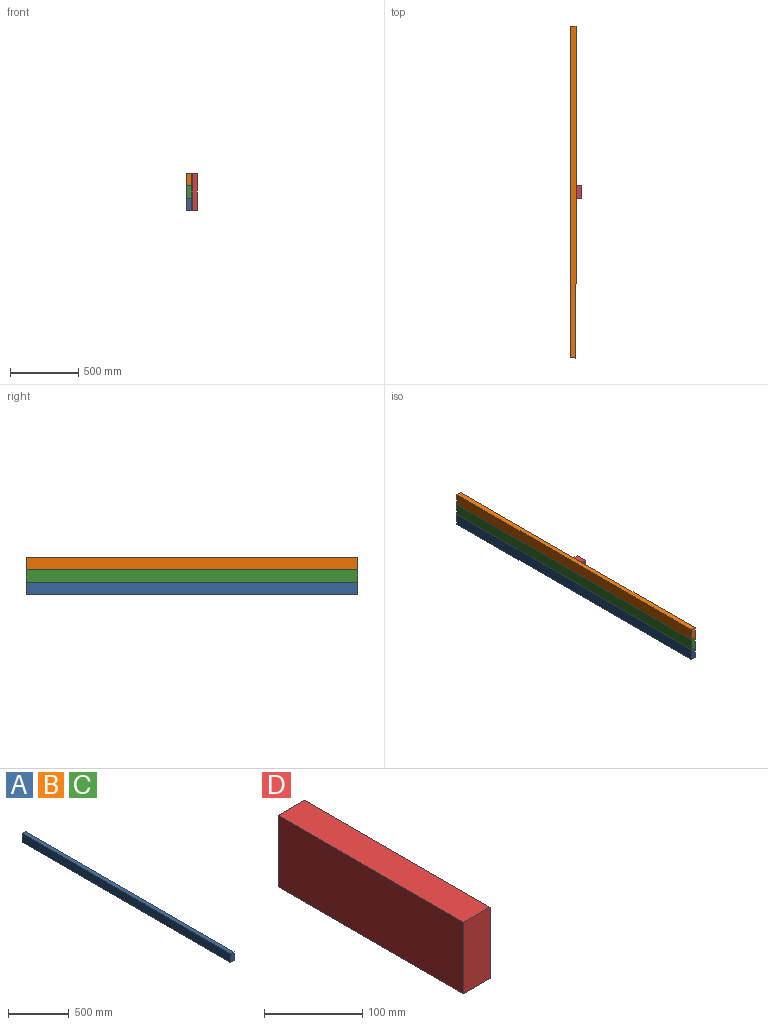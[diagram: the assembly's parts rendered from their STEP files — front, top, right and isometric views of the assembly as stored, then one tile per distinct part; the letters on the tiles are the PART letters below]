
ASSEMBLY  parts=4 mates=3
PART A: 6 faces, bbox 38.1x2438.4x88.9 mm
  f0: plane 2438.4x38.1mm, normal (0,0,1), area 92903mm2, adj f1,f3,f4,f5
  f1: plane 2438.4x88.9mm, normal (-1,0,0), area 216773.8mm2, adj f0,f2,f4,f5
  f2: plane 2438.4x38.1mm, normal (0,0,-1), area 92903mm2, adj f1,f3,f4,f5
  f3: plane 2438.4x88.9mm, normal (1,0,0), area 216773.8mm2, adj f0,f2,f4,f5
  f4: plane 88.9x38.1mm, normal (0,-1,0), area 3387.1mm2, adj f0,f1,f2,f3
  f5: plane 88.9x38.1mm, normal (0,1,0), area 3387.1mm2, adj f0,f1,f2,f3
PART B: same geometry as A
PART C: same geometry as A
PART D: 6 faces, bbox 38.1x266.7x88.9 mm
  f0: plane 266.7x38.1mm, normal (0,0,1), area 10161.3mm2, adj f1,f3,f4,f5
  f1: plane 266.7x88.9mm, normal (-1,0,0), area 23709.6mm2, adj f0,f2,f4,f5
  f2: plane 266.7x38.1mm, normal (0,0,-1), area 10161.3mm2, adj f1,f3,f4,f5
  f3: plane 266.7x88.9mm, normal (1,0,0), area 23709.6mm2, adj f0,f2,f4,f5
  f4: plane 88.9x38.1mm, normal (0,-1,0), area 3387.1mm2, adj f0,f1,f2,f3
  f5: plane 88.9x38.1mm, normal (0,1,0), area 3387.1mm2, adj f0,f1,f2,f3
PLACE A t=(-434.98,191.68,-159.44)mm
PLACE B rot(axis=(-1,0,0),180deg) t=(-434.98,191.68,18.36)mm
PLACE C t=(-434.98,191.68,-70.54)mm
PLACE D rot(axis=(0,0.71,0.71),180deg) t=(-396.88,191.68,-70.54)mm
MATE fastened C.f2 <-> A.f0  axis (0,0,-1) through (-434.98,191.68,-114.99)mm
MATE fastened C.f0 <-> B.f0  axis (0,0,1) through (-434.98,191.68,-26.09)mm
MATE fastened D.f3 <-> C.f3  axis (-1,0,0) through (-415.93,191.68,-70.54)mm
